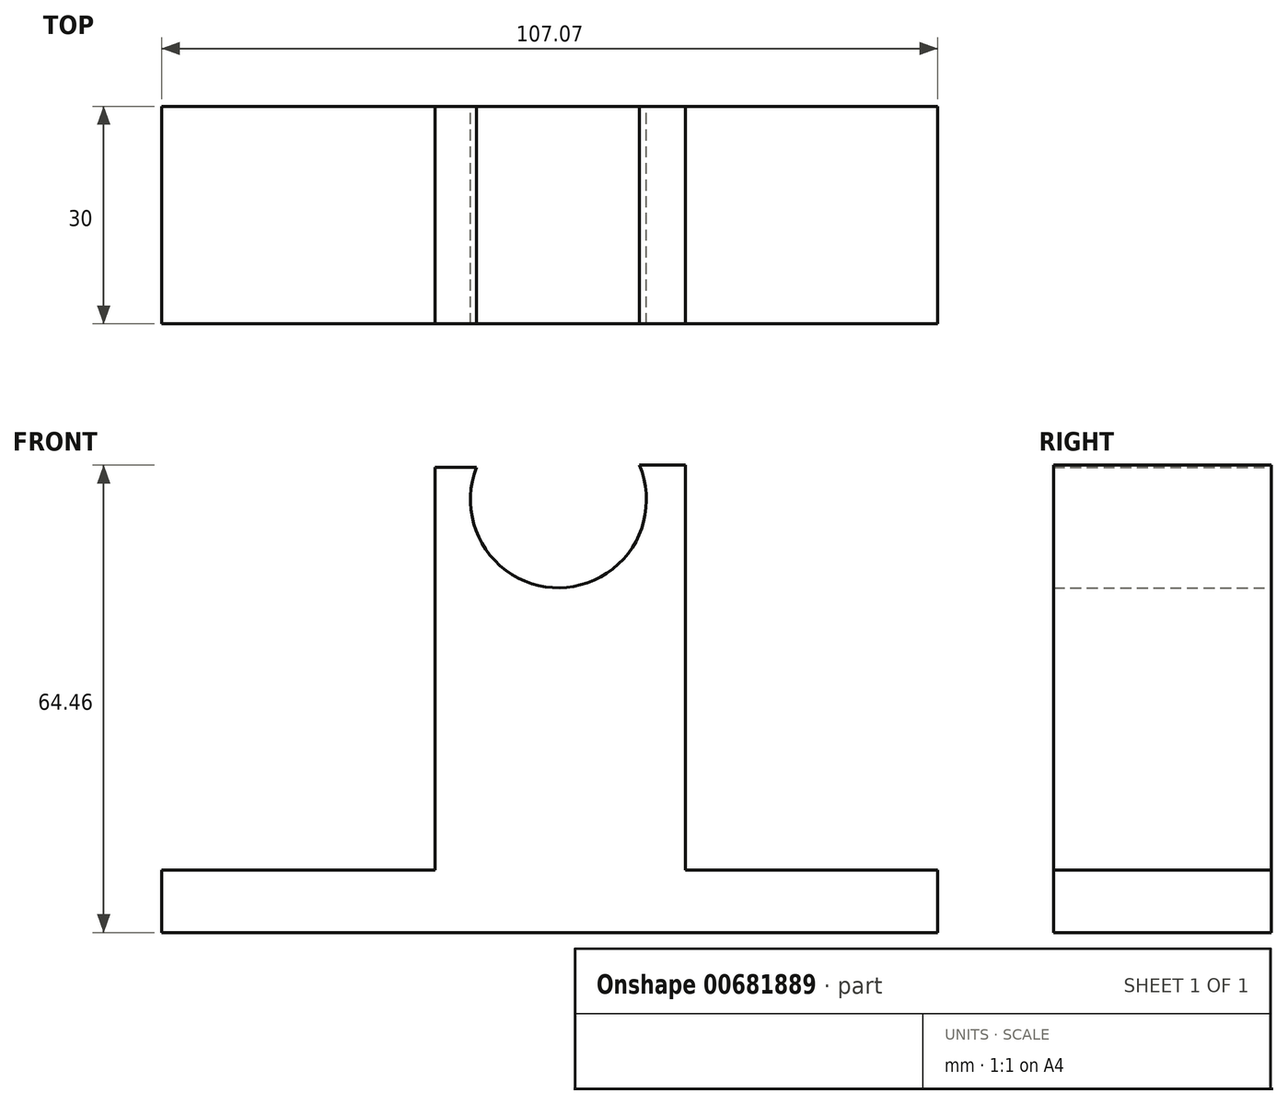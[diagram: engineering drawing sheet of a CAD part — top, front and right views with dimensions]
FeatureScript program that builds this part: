
annotation { "Feature Type Name" : "Feature", "Feature Type Description" : "" }
export const myFeature = defineFeature(function(context is Context, id is Id, definition is map)
    precondition{}
    {
        {
            var Q0;
            Q0=qCreatedBy(makeId("Front.planeOp"),FACE);
            var sketch = newSketch(context, id + "F0", { "sketchPlane" : qUnion([Q0])});
            skLineSegment(sketch, "E0", {"start": v(-19.71, -32.1) * mm, "end": v(-57.42, -32.1) * mm});
            skLineSegment(sketch, "E1", {"start": v(-57.42, -32.1) * mm, "end": v(-57.42, -40.72) * mm});
            skLineSegment(sketch, "E2", {"start": v(-57.42, -40.72) * mm, "end": v(49.65, -40.72) * mm});
            skLineSegment(sketch, "E3", {"start": v(49.65, -40.72) * mm, "end": v(49.65, -32.1) * mm});
            skLineSegment(sketch, "E4", {"start": v(49.65, -32.1) * mm, "end": v(14.82, -32.1) * mm});
            skLineSegment(sketch, "E5", {"start": v(14.82, -32.1) * mm, "end": v(14.82, 23.74) * mm});
            skLineSegment(sketch, "E6", {"start": v(14.82, 23.74) * mm, "end": v(8.5, 23.74) * mm});
            skLineSegment(sketch, "E7", {"start": v(-19.71, -32.1) * mm, "end": v(-19.71, 23.46) * mm});
            skLineSegment(sketch, "E8", {"start": v(-19.71, 23.46) * mm, "end": v(-13.96, 23.46) * mm});
            skArc(sketch, "E9", {"start": v(-13.96, 23.46) * mm, "mid": v(-2.52, 6.84) * mm, "end": v(8.5, 23.74) * mm});
            skSolve(sketch);
        }
        {
            var Q0;
            Q0 = qSketchRegion(id + "F0", true);
            extrude(context, id + "F1", {"entities" : qUnion([Q0]), "depth" : 30 * mm, "offsetDistance" : 25 * mm});
        }
    });
